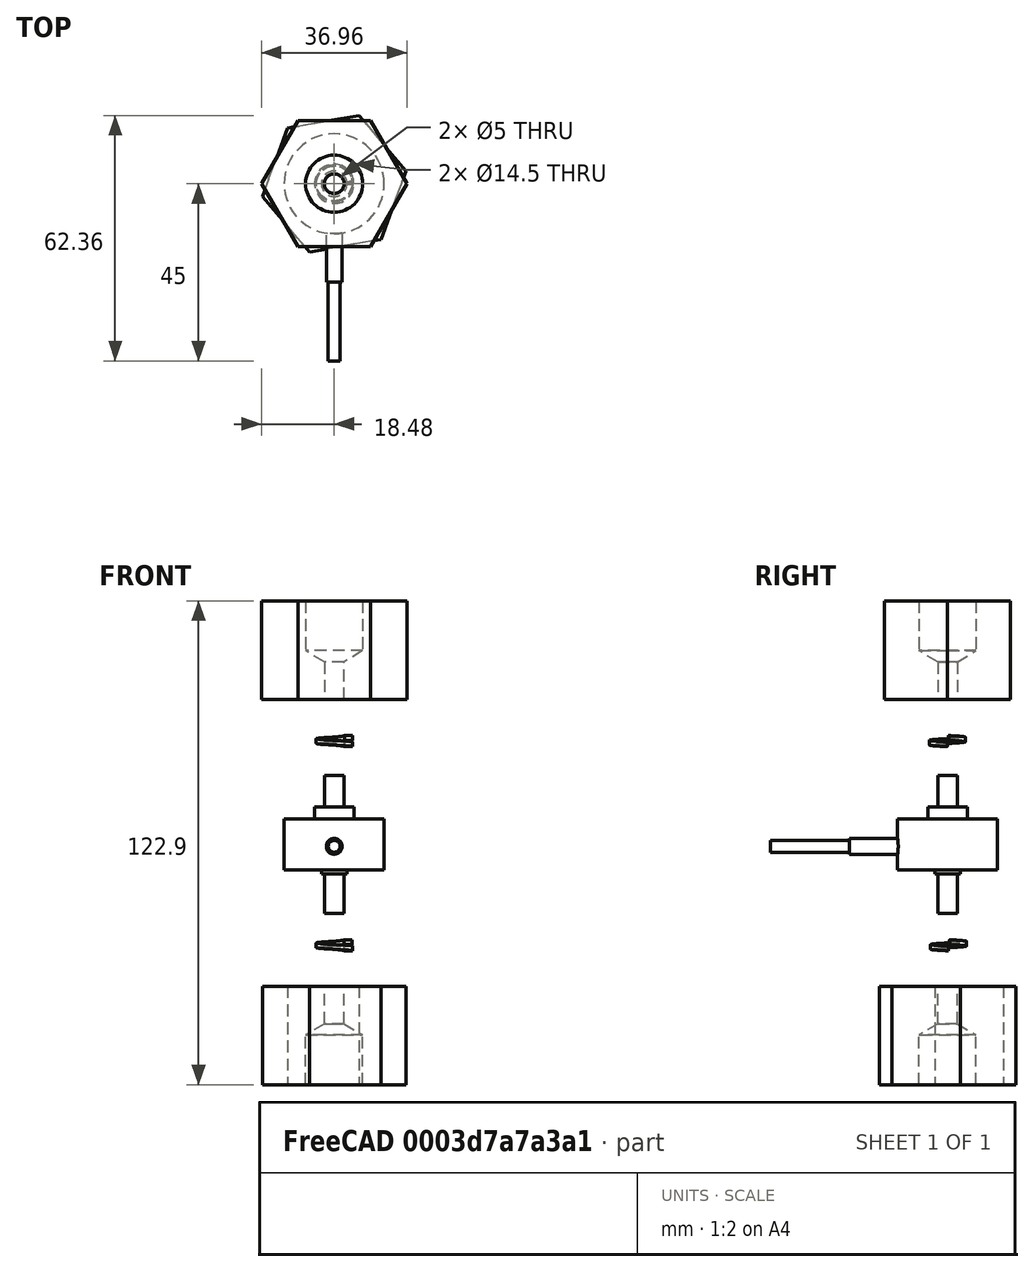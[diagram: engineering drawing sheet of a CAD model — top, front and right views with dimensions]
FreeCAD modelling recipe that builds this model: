
FCSTD DOCUMENT  (FreeCAD 0.19R24267 +99 (Git))
Label: Assembly step 3A
License: All rights reserved
LicenseURL: http://en.wikipedia.org/wiki/All_rights_reserved
objects: Part::FeaturePython×5, App::FeaturePython×4, Part::Mirroring×2
note: 7 computed .brp shape members not serialized (recipe doc carries the construction recipe); baked Part::Feature solids carry a one-line shape summary decoded from their .brp

FEATURE [Part::FeaturePython] b_50kg_load_cell_001_  label="50kg load cell_001"  # a2plus imported part (geometry in sourceFile) (typed FeaturePython)
  Placement = pos=(0,0,22) rot=(0,0,1;0rad)
  a2p_Version = 0.4.60g
  fixedPosition = true
  objectType = a2pPart
  sourceFile = .\50kg load cell.FCStd
  subassemblyImport = false
  timeLastImport = 1.69203e+09
  updateColors = true
FEATURE [Part::FeaturePython] b_V2_Thread_adapter_blank_low_load_001_  label="V2 Thread adapter blank low load_001"  # a2plus imported part (geometry in sourceFile) (typed FeaturePython)
  Placement = pos=(0,0,65.35) rot=(0,0,1;0rad)
  a2p_Version = 0.4.60g
  fixedPosition = false
  objectType = a2pPart
  sourceFile = .\..\Load cell and clamp mounting - part designs\V2 Thread adapter blank low load.FCStd
  subassemblyImport = false
  timeLastImport = 1.69209e+09
  updateColors = true
FEATURE [App::FeaturePython] axisCoincident_001  label="axisCoincident_001__V2 Thread adapter blank low load_001"  # a2plus constraint (typed FeaturePython)
  Object1 = b_50kg_load_cell_001_
  Object2 = b_V2_Thread_adapter_blank_low_load_001_
  ParentTreeObject = -> b_50kg_load_cell_001_
  SubElement1 = Face12
  SubElement2 = Face9
  Suppressed = false
  Type = axial
  directionConstraint = 0
  lockRotation = false
FEATURE [App::FeaturePython] axisCoincident_001_mirror  label="axisCoincident_001__50kg load cell_001"  # a2plus constraint (typed FeaturePython)
  Object1 = b_50kg_load_cell_001_
  Object2 = b_V2_Thread_adapter_blank_low_load_001_
  ParentTreeObject = -> b_V2_Thread_adapter_blank_low_load_001_
  SubElement1 = Face12
  SubElement2 = Face9
  Suppressed = false
  Type = axial
  directionConstraint = 0
  lockRotation = false
FEATURE [Part::FeaturePython] b_V2_Thread_adapter_blank_low_load_001_001  label="V2 Thread adapter blank low load_002"  # a2plus imported part (geometry in sourceFile) (typed FeaturePython)
  Placement = pos=(2.3431e-07,1.64072e-07,-7.55) rot=(-0.57359,0.819142,0;3.14159rad)
  a2p_Version = 0.4.60g
  fixedPosition = false
  objectType = a2pPart
  sourceFile = .\..\Load cell and clamp mounting - part designs\V2 Thread adapter blank low load.FCStd
  subassemblyImport = false
  timeLastImport = 1.69209e+09
  updateColors = true
FEATURE [App::FeaturePython] axisCoincident_002  label="axisCoincident_002__V2 Thread adapter blank low load_002"  # a2plus constraint (typed FeaturePython)
  Object1 = b_50kg_load_cell_001_
  Object2 = b_V2_Thread_adapter_blank_low_load_001_001
  ParentTreeObject = -> b_50kg_load_cell_001_
  SubElement1 = Face11
  SubElement2 = Face9
  Suppressed = false
  Type = axial
  directionConstraint = 0
  lockRotation = false
FEATURE [App::FeaturePython] axisCoincident_002_mirror  label="axisCoincident_002__50kg load cell_001"  # a2plus constraint (typed FeaturePython)
  Object1 = b_50kg_load_cell_001_
  Object2 = b_V2_Thread_adapter_blank_low_load_001_001
  ParentTreeObject = -> b_V2_Thread_adapter_blank_low_load_001_001
  SubElement1 = Face11
  SubElement2 = Face9
  Suppressed = false
  Type = axial
  directionConstraint = 0
  lockRotation = false
FEATURE [Part::FeaturePython] b_TR_Fastenings_Ltd_M5_Single_Coil_Washer_Rectangular_DIN_127B1_001_  label="TR Fastenings Ltd-M5 Single Coil Washer Rectangular DIN 127B1_001"  # a2plus imported part (geometry in sourceFile) (typed FeaturePython)
  Placement = pos=(0.0178875,-0.00955811,52.7393) rot=(0,0,1;0rad)
  a2p_Version = 0.4.60g
  fixedPosition = false
  objectType = a2pPart
  sourceFile = .\..\Common TR fastners - supporting models\TR Fastenings Ltd-M5 Single Coil Washer Rectangular DIN 127B.step
  subassemblyImport = false
  timeLastImport = 1.69265e+09
  updateColors = true
FEATURE [Part::FeaturePython] b_TR_Fastenings_Ltd_M5_Single_Coil_Washer_Rectangular_DIN_127B1_001_001  label="TR Fastenings Ltd-M5 Single Coil Washer Rectangular DIN 127B1_002"  # a2plus imported part (geometry in sourceFile) (typed FeaturePython)
  Placement = pos=(-0.0105007,0.0259134,6.40987) rot=(0,0,1;0rad)
  a2p_Version = 0.4.60g
  fixedPosition = false
  objectType = a2pPart
  sourceFile = .\..\Common TR fastners - supporting models\TR Fastenings Ltd-M5 Single Coil Washer Rectangular DIN 127B.step
  subassemblyImport = false
  timeLastImport = 1.69265e+09
  updateColors = true
FEATURE [Part::Mirroring] Part__Mirroring  label="TR Fastenings Ltd-M5 Single Coil Washer Rectangular DIN 127B1_001 (Mirror #1)"
  Base = (0,0,0)
  Normal = (0,0,1)
  Placement = pos=(0.0213699,-0.0181123,106.675) rot=(0,0,1;0rad)
  Source = -> b_TR_Fastenings_Ltd_M5_Single_Coil_Washer_Rectangular_DIN_127B1_001_
FEATURE [Part::Mirroring] Part__Mirroring001  label="TR Fastenings Ltd-M5 Single Coil Washer Rectangular DIN 127B1_002 (Mirror #2)"
  Base = (0,0,0)
  Normal = (0,0,1)
  Placement = pos=(0.0213604,0.192185,8.46031) rot=(0,0,1;0rad)
  Source = -> b_TR_Fastenings_Ltd_M5_Single_Coil_Washer_Rectangular_DIN_127B1_001_001
